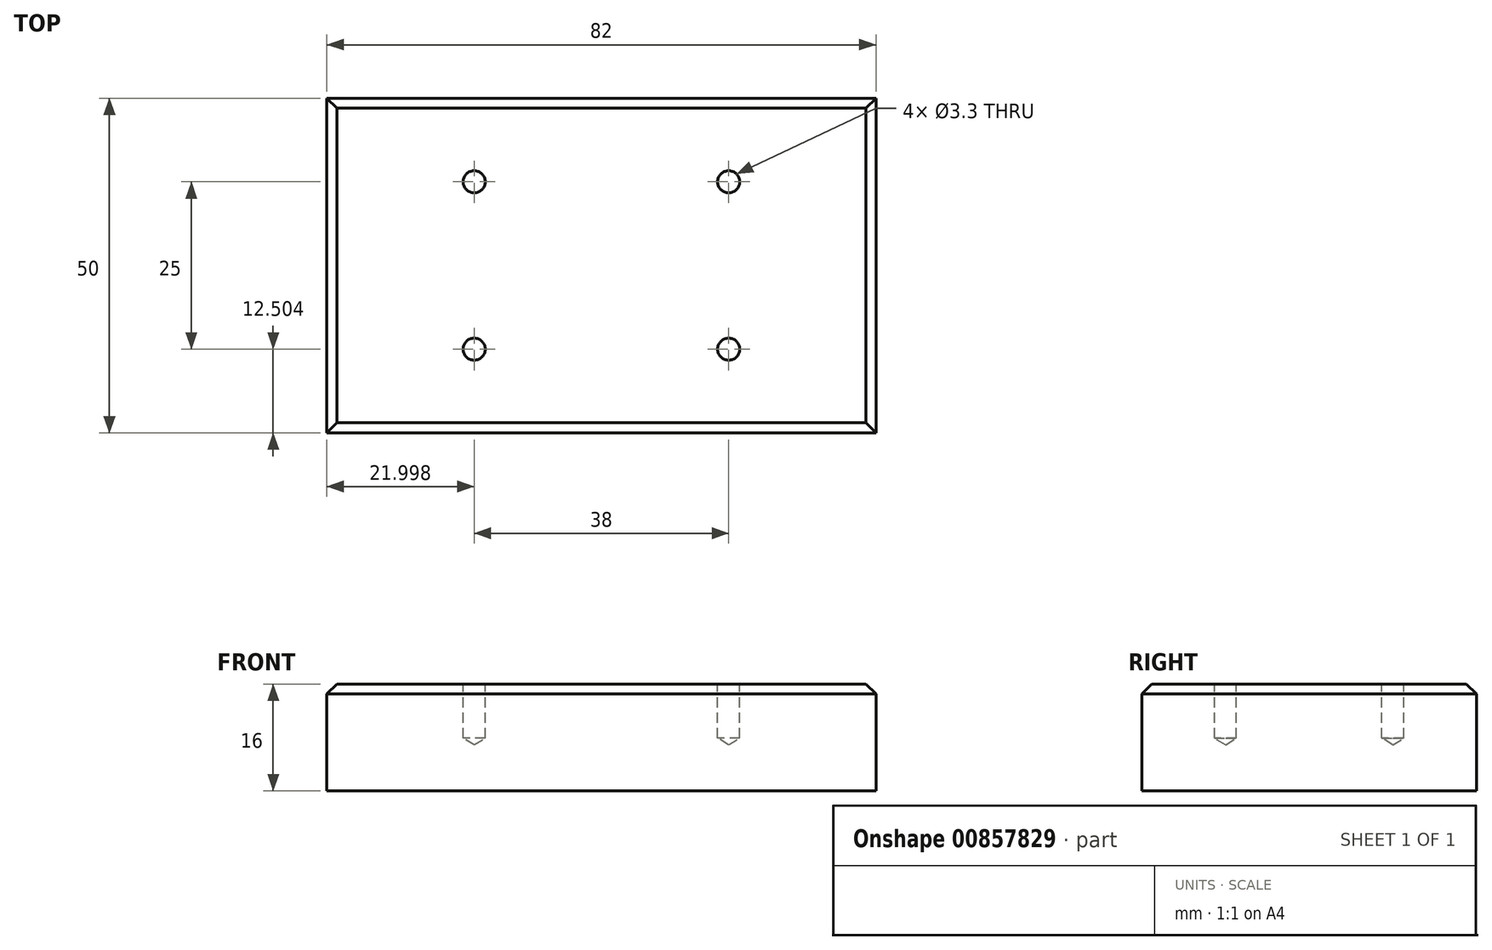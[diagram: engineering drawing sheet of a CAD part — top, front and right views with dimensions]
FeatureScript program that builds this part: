
annotation { "Feature Type Name" : "Feature", "Feature Type Description" : "" }
export const myFeature = defineFeature(function(context is Context, id is Id, definition is map)
    precondition{}
    {
        {
            var Q0;
            Q0=qCreatedBy(makeId("Top.planeOp"),FACE);
            var sketch = newSketch(context, id + "F0", { "sketchPlane" : qUnion([Q0])});
            skLineSegment(sketch, "E0.bottom", {"start": v(-27.3, 27.3) * mm, "end": v(54.7, 27.3) * mm});
            skLineSegment(sketch, "E0.top", {"start": v(-27.3, -22.7) * mm, "end": v(54.7, -22.7) * mm});
            skLineSegment(sketch, "E0.left", {"start": v(-27.3, 27.3) * mm, "end": v(-27.3, -22.7) * mm});
            skLineSegment(sketch, "E0.right", {"start": v(54.7, 27.3) * mm, "end": v(54.7, -22.7) * mm});
            skSolve(sketch);
        }
        {
            var Q0;
            Q0=makeQuery(id+"F0.imprint","IMPRINT",FACE,{"disambiguationData":[TD([[makeQuery(id+"F0.imprint","IMPRINT",EDGE,{"derivedFrom":sQuery(id+"F0.wireOp",EDGE,"E0.bottom")}),-1.0]])]});
            extrude(context, id + "F1", {"entities" : qUnion([Q0]), "depth" : 16 * mm, "offsetDistance" : 25 * mm});
        }
        {
            var Q0;
            Q0=makeQuery(id+"F1.opExtrude","CAP_FACE",FACE,{"disambiguationData":[OSD([sQuery(id+"F0.wireOp",EDGE,"E0.bottom"),sQuery(id+"F0.wireOp",EDGE,"E0.top"),sQuery(id+"F0.wireOp",EDGE,"E0.left"),sQuery(id+"F0.wireOp",EDGE,"E0.right")])],"isStart":false});
            chamfer(context, id + "F2", {"entities" : qUnion([Q0]), "width" : 1.5 * mm, "tangentPropagation" : true});
        }
        {
            var Q0;
            Q0=makeQuery(id+"F1.opExtrude","CAP_FACE",FACE,{"disambiguationData":[OSD([sQuery(id+"F0.wireOp",EDGE,"E0.bottom"),sQuery(id+"F0.wireOp",EDGE,"E0.top"),sQuery(id+"F0.wireOp",EDGE,"E0.left"),sQuery(id+"F0.wireOp",EDGE,"E0.right")])],"isStart":false});
            var sketch = newSketch(context, id + "F3", { "sketchPlane" : qUnion([Q0])});
            skPoint(sketch, "E1", {"position": v(-5.3, 14.8) * mm});
            skPoint(sketch, "E2", {"position": v(32.7, 14.8) * mm});
            skPoint(sketch, "E3", {"position": v(32.7, -10.2) * mm});
            skPoint(sketch, "E4", {"position": v(-5.3, -10.2) * mm});
            skSolve(sketch);
        }
        {
            var Q0;
            Q0=sQuery(id+"F3.wireOp",VERTEX,"E1");
            var Q1;
            Q1=sQuery(id+"F3.wireOp",VERTEX,"E4");
            var Q2;
            Q2=sQuery(id+"F3.wireOp",VERTEX,"E2");
            var Q3;
            Q3=sQuery(id+"F3.wireOp",VERTEX,"E3");
            var Q4;
            Q4=makeQuery(id+"F1.opExtrude","SWEPT_BODY",BODY,{"disambiguationData":[OSD([sQuery(id+"F0.wireOp",EDGE,"E0.bottom"),sQuery(id+"F0.wireOp",EDGE,"E0.top"),sQuery(id+"F0.wireOp",EDGE,"E0.left"),sQuery(id+"F0.wireOp",EDGE,"E0.right")])]});
            hole(context, id + "F4", {"style" : HoleStyle.SIMPLE, "endStyle" : HoleEndStyle.BLIND, "standardTappedOrClearance" : lookupTablePath({ "standard" : "ISO", "engagement" : "75%", "pitch" : "0.7 mm", "size" : "M4", "type" : "Tapped" }), "standardBlindInLast" : lookupTablePath({ "standard" : "ISO", "engagement" : "75%", "pitch" : "0.7 mm", "size" : "M4", "type" : "Tapped" }), "holeDiameter" : 3.3 * mm, "majorDiameter" : 4 * mm, "showTappedDepth" : true, "holeDepth" : 8.1 * mm, "isTappedThrough" : true, "tappedDepth" : 6 * mm, "tapClearance" : 3, "locations" : qUnion([Q0, Q1, Q2, Q3]), "scope" : qUnion([Q4])});
        }
    });
